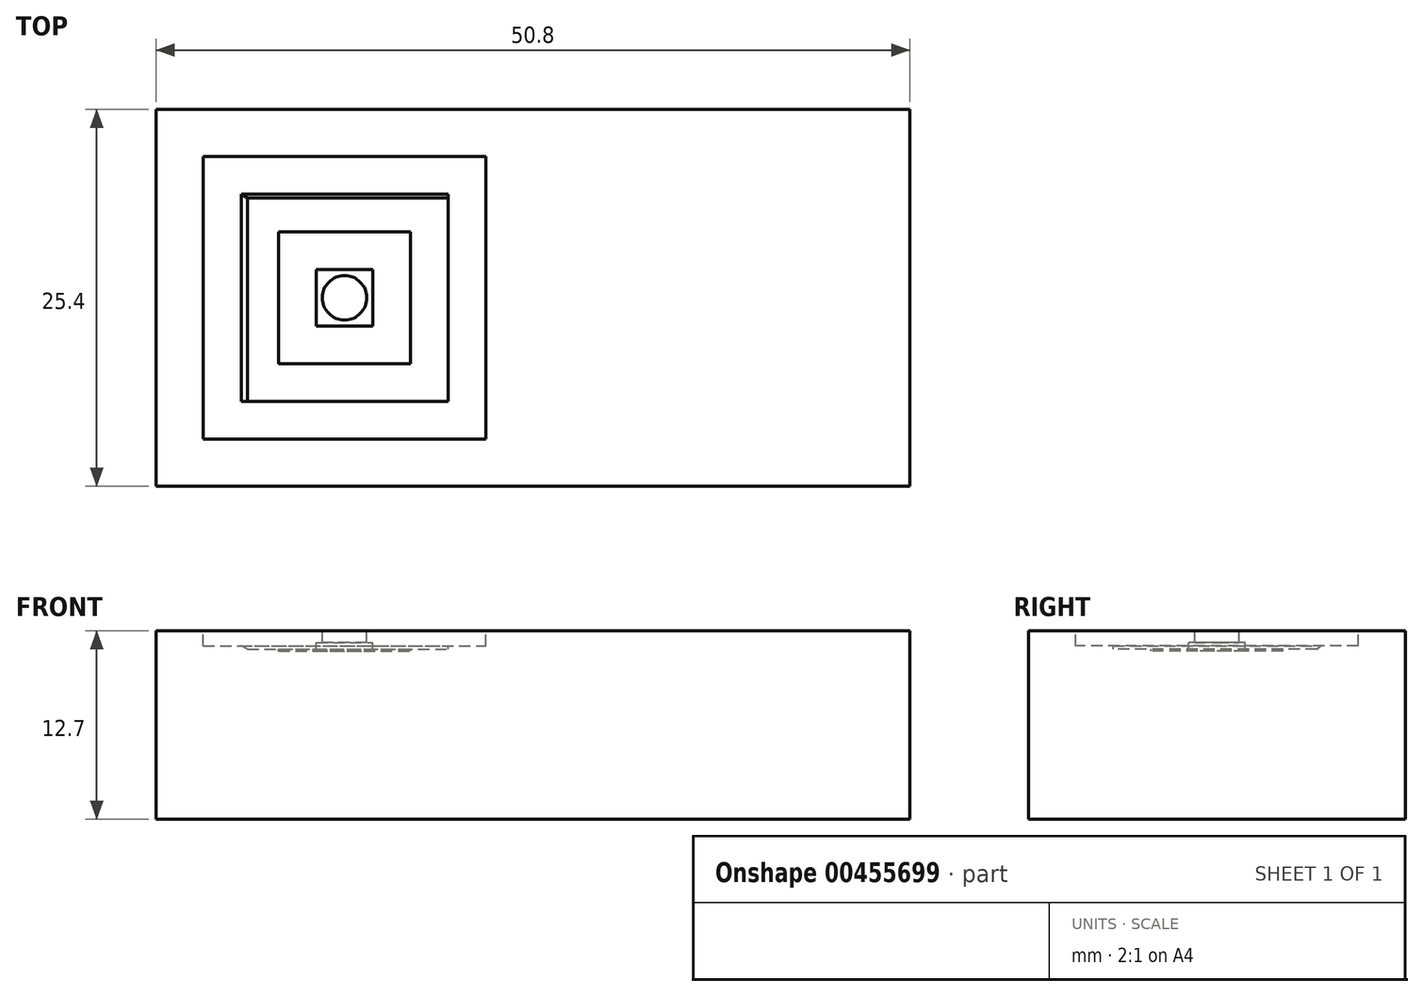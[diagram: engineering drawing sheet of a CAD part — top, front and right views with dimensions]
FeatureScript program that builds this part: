
annotation { "Feature Type Name" : "Feature", "Feature Type Description" : "" }
export const myFeature = defineFeature(function(context is Context, id is Id, definition is map)
    precondition{}
    {
        {
            var Q0;
            Q0=qCreatedBy(makeId("Top.planeOp"),FACE);
            var sketch = newSketch(context, id + "F0", { "sketchPlane" : qUnion([Q0])});
            skLineSegment(sketch, "E0.bottom", {"start": v(25.4, 12.7) * mm, "end": v(-25.4, 12.7) * mm});
            skLineSegment(sketch, "E0.top", {"start": v(25.4, -12.7) * mm, "end": v(-25.4, -12.7) * mm});
            skLineSegment(sketch, "E0.left", {"start": v(25.4, 12.7) * mm, "end": v(25.4, -12.7) * mm});
            skLineSegment(sketch, "E0.right", {"start": v(-25.4, 12.7) * mm, "end": v(-25.4, -12.7) * mm});
            skPoint(sketch, "E0.middle", {"position": v(0, 0) * mm});
            skSolve(sketch);
        }
        {
            var Q0;
            Q0=makeQuery(id+"F0.imprint","IMPRINT",FACE,{"disambiguationData":[TD([[makeQuery(id+"F0.imprint","IMPRINT",EDGE,{"derivedFrom":sQuery(id+"F0.wireOp",EDGE,"E0.bottom")}),1.0]])]});
            extrude(context, id + "F1", {"entities" : qUnion([Q0]), "depth" : 12.7 * mm, "offsetDistance" : 25.4 * mm});
        }
        {
            var Q0;
            Q0=makeQuery(id+"F1.opExtrude","CAP_FACE",FACE,{"disambiguationData":[OSD([sQuery(id+"F0.wireOp",EDGE,"E0.bottom"),sQuery(id+"F0.wireOp",EDGE,"E0.top"),sQuery(id+"F0.wireOp",EDGE,"E0.left"),sQuery(id+"F0.wireOp",EDGE,"E0.right")])],"isStart":false});
            var sketch = newSketch(context, id + "F2", { "sketchPlane" : qUnion([Q0])});
            skLineSegment(sketch, "E1.0", {"start": v(25.4, 12.7) * mm, "end": v(-25.4, 12.7) * mm});
            skLineSegment(sketch, "E1.1", {"start": v(-25.4, 12.7) * mm, "end": v(-25.4, -12.7) * mm});
            skLineSegment(sketch, "E1.2", {"start": v(25.4, -12.7) * mm, "end": v(-25.4, -12.7) * mm});
            skLineSegment(sketch, "E1.3", {"start": v(25.4, 12.7) * mm, "end": v(25.4, -12.7) * mm});
            skLineSegment(sketch, "E2.bottom", {"start": v(-22.23, 9.53) * mm, "end": v(-3.18, 9.53) * mm});
            skLineSegment(sketch, "E2.top", {"start": v(-22.23, -9.53) * mm, "end": v(-3.18, -9.53) * mm});
            skLineSegment(sketch, "E2.left", {"start": v(-22.23, 9.53) * mm, "end": v(-22.23, -9.53) * mm});
            skLineSegment(sketch, "E2.right", {"start": v(-3.18, 9.53) * mm, "end": v(-3.18, -9.53) * mm});
            skLineSegment(sketch, "E3.0", {"start": v(-19.69, 6.99) * mm, "end": v(-5.72, 6.99) * mm});
            skLineSegment(sketch, "E3.1", {"start": v(-19.69, 6.99) * mm, "end": v(-19.69, -6.99) * mm});
            skLineSegment(sketch, "E3.2", {"start": v(-19.69, -6.99) * mm, "end": v(-5.72, -6.99) * mm});
            skLineSegment(sketch, "E3.3", {"start": v(-5.72, 6.99) * mm, "end": v(-5.72, -6.99) * mm});
            skLineSegment(sketch, "E4.0", {"start": v(-17.14, 4.44) * mm, "end": v(-8.26, 4.44) * mm});
            skLineSegment(sketch, "E4.1", {"start": v(-17.14, 4.44) * mm, "end": v(-17.14, -4.44) * mm});
            skLineSegment(sketch, "E4.2", {"start": v(-17.14, -4.44) * mm, "end": v(-8.26, -4.44) * mm});
            skLineSegment(sketch, "E4.3", {"start": v(-8.26, 4.44) * mm, "end": v(-8.26, -4.44) * mm});
            skLineSegment(sketch, "E5.0", {"start": v(-14.6, 1.9) * mm, "end": v(-10.8, 1.9) * mm});
            skLineSegment(sketch, "E5.1", {"start": v(-14.6, 1.9) * mm, "end": v(-14.6, -1.9) * mm});
            skLineSegment(sketch, "E5.2", {"start": v(-14.6, -1.9) * mm, "end": v(-10.8, -1.9) * mm});
            skLineSegment(sketch, "E5.3", {"start": v(-10.8, 1.9) * mm, "end": v(-10.8, -1.9) * mm});
            skSolve(sketch);
        }
        {
            var Q0;
            Q0=makeQuery(id+"F2.imprint","IMPRINT",FACE,{"disambiguationData":[TD([[makeQuery(id+"F2.imprint","IMPRINT",EDGE,{"derivedFrom":sQuery(id+"F2.wireOp",EDGE,"E2.bottom")}),-1.0]])]});
            var Q1;
            Q1=makeQuery(id+"F2.imprint","IMPRINT",FACE,{"disambiguationData":[TD([[makeQuery(id+"F2.imprint","IMPRINT",EDGE,{"derivedFrom":sQuery(id+"F2.wireOp",EDGE,"E3.0")}),-1.0]])]});
            var Q2;
            Q2=makeQuery(id+"F2.imprint","IMPRINT",FACE,{"disambiguationData":[TD([[makeQuery(id+"F2.imprint","IMPRINT",EDGE,{"derivedFrom":sQuery(id+"F2.wireOp",EDGE,"E4.0")}),-1.0]])]});
            extrude(context, id + "F3", {"entities" : qUnion([Q0, Q1, Q2]), "operationType" : NewBodyOperationType.REMOVE, "oppositeDirection" : true, "depth" : 1 * mm, "offsetDistance" : 25.4 * mm});
        }
        {
            var Q0;
            Q0=makeQuery(id+"F2.imprint","IMPRINT",FACE,{"disambiguationData":[TD([[makeQuery(id+"F2.imprint","IMPRINT",EDGE,{"derivedFrom":sQuery(id+"F2.wireOp",EDGE,"E3.0")}),-1.0]])]});
            extrude(context, id + "F4", {"entities" : qUnion([Q0]), "operationType" : NewBodyOperationType.REMOVE, "oppositeDirection" : true, "depth" : 1.25 * mm, "offsetDistance" : 25.4 * mm});
        }
        {
            var Q0;
            Q0=makeQuery(id+"F2.imprint","IMPRINT",FACE,{"disambiguationData":[TD([[makeQuery(id+"F2.imprint","IMPRINT",EDGE,{"derivedFrom":sQuery(id+"F2.wireOp",EDGE,"E4.0")}),-1.0]])]});
            extrude(context, id + "F5", {"entities" : qUnion([Q0]), "operationType" : NewBodyOperationType.REMOVE, "oppositeDirection" : true, "depth" : 1.35 * mm, "offsetDistance" : 25 * mm});
        }
        {
            var Q0;
            Q0=makeQuery(id+"F4.boolean.opBoolean","COPY",EDGE,{"derivedFrom":makeQuery(id+"F4.opExtrude","CAP_EDGE",EDGE,{"disambiguationData":[OSD([sQuery(id+"F2.wireOp",EDGE,"E3.0")])],"isStart":false})});
            chamfer(context, id + "F6", {"entities" : qUnion([Q0]), "chamferType" : ChamferType.OFFSET_ANGLE, "width" : 0.25 * mm, "oppositeDirection" : false, "angle" : 45 * degree, "tangentPropagation" : true});
        }
        {
            var Q0;
            Q0=makeQuery(id+"F4.boolean.opBoolean","COPY",EDGE,{"derivedFrom":makeQuery(id+"F4.opExtrude","CAP_EDGE",EDGE,{"disambiguationData":[OSD([sQuery(id+"F2.wireOp",EDGE,"E3.1")])],"isStart":false})});
            chamfer(context, id + "F7", {"entities" : qUnion([Q0]), "chamferType" : ChamferType.OFFSET_ANGLE, "width" : 0.45 * mm, "oppositeDirection" : false, "angle" : 30 * degree, "tangentPropagation" : true});
        }
        {
            var Q0;
            Q0=makeQuery(id+"F2.imprint","IMPRINT",FACE,{"disambiguationData":[TD([[makeQuery(id+"F2.imprint","IMPRINT",EDGE,{"derivedFrom":sQuery(id+"F2.wireOp",EDGE,"E5.0")}),-1.0]])]});
            var sketch = newSketch(context, id + "F8", { "sketchPlane" : qUnion([Q0])});
            skLineSegment(sketch, "E6.0.0", {"start": v(-10.8, -1.9) * mm, "end": v(-10.8, 1.9) * mm});
            skLineSegment(sketch, "E6.0.1", {"start": v(-10.8, 1.9) * mm, "end": v(-14.6, 1.9) * mm});
            skLineSegment(sketch, "E6.0.2", {"start": v(-14.6, 1.9) * mm, "end": v(-14.6, -1.9) * mm});
            skLineSegment(sketch, "E6.0.3", {"start": v(-14.6, -1.9) * mm, "end": v(-10.8, -1.9) * mm});
            skLineSegment(sketch, "E7", {"start": v(-14.6, 1.9) * mm, "end": v(-10.8, -1.9) * mm, "construction": true});
            skLineSegment(sketch, "E8", {"start": v(-10.8, 1.9) * mm, "end": v(-14.6, -1.9) * mm, "construction": true});
            skCircle(sketch, "E9", {"center": v(-12.7, 0) * mm, "radius": 1.5 * mm});
            skSolve(sketch);
        }
        {
            var Q0;
            Q0=makeQuery(id+"F8.imprint","IMPRINT",FACE,{"disambiguationData":[TD([[makeQuery(id+"F8.imprint","IMPRINT",EDGE,{"derivedFrom":sQuery(id+"F8.wireOp",EDGE,"E6.0.0")}),-1.0]])]});
            extrude(context, id + "F9", {"entities" : qUnion([Q0]), "operationType" : NewBodyOperationType.REMOVE, "oppositeDirection" : true, "depth" : 0.8 * mm, "offsetDistance" : 25 * mm});
        }
    });
